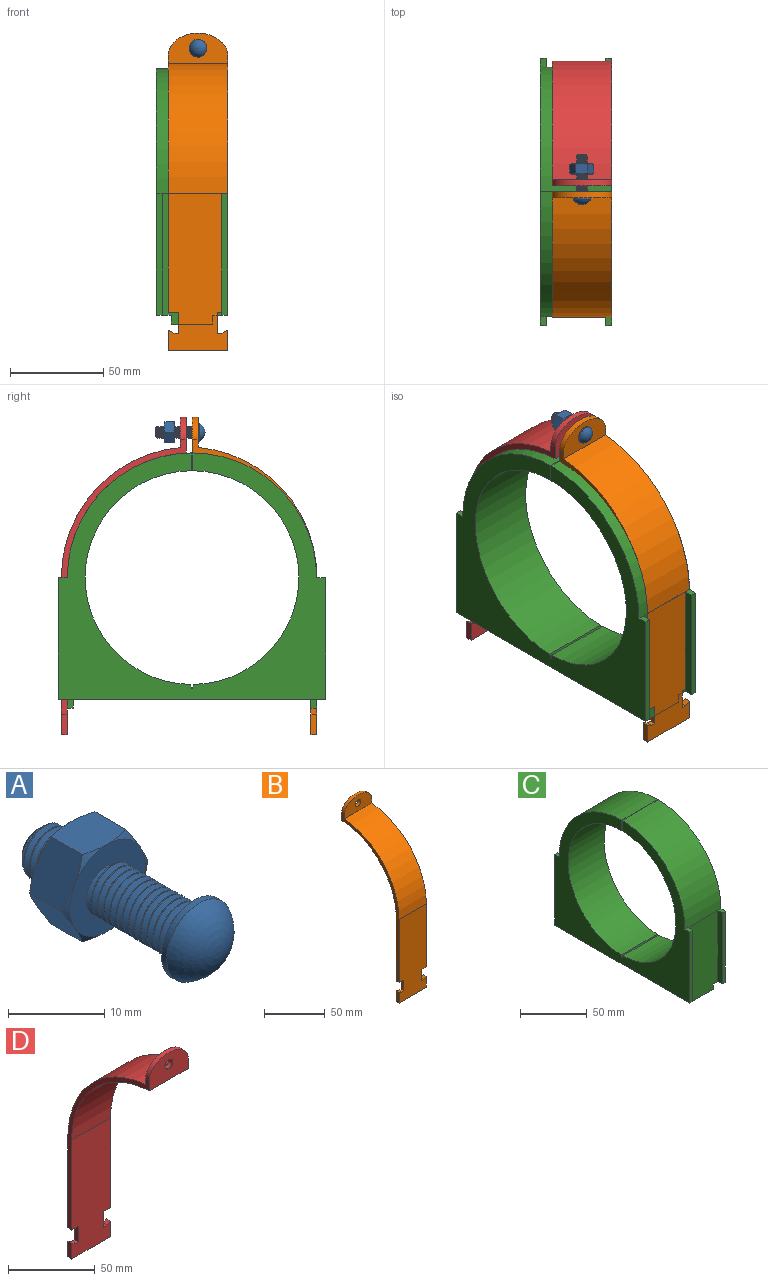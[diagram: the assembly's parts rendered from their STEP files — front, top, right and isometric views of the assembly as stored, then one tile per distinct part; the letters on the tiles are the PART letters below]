
ASSEMBLY  parts=4 mates=3
PART A: 34 faces, bbox 13.4x27.4x13.4 mm
  f0: cylinder r=3.17mm len=12.7mm, axis (0,-1,0), area 31.8mm2, adj f1,f3,f4,f8
  f1: bspline ~13.49x6.35mm, area 172.8mm2, adj f0,f2,f4,f8
  f2: cylinder r=2.59mm len=12.7mm, axis (0,-1,0), area 25.9mm2, adj f1,f3,f4,f8
  f3: bspline ~13.49x6.35mm, area 172.8mm2, adj f0,f2,f4,f8
  f4: plane 9.89x9.89mm, normal (0,1,0), area 45.1mm2, adj f0,f1,f2,f3,f5
  f5: cylinder r=4.76mm len=9.53mm, axis (0,1,0), area 22.8mm2, adj f4,f6
  f6: sphere r=5.32mm, area 98.5mm2, adj f5
  f7: plane 11.47x11.47mm, normal (0,1,0), area 70.8mm2, adj f15,f16,f17,f18,f19,f20,f30,f31
  f8: plane 11.47x11.47mm, normal (0,-1,0), area 70.8mm2, adj f0,f1,f2,f3,f21,f22,f23,f24
  f9: plane 6.09x6.08mm, normal (-0.87,0,0.5), area 33.4mm2, adj f10,f14,f15,f16,f21,f22
  f10: plane 6.95x6.08mm, normal (0,0,1), area 33.4mm2, adj f9,f11,f15,f20,f21,f26
  f11: plane 6.09x6.08mm, normal (0.87,0,0.5), area 33.4mm2, adj f10,f12,f19,f20,f25,f26
  f12: plane 6.09x6.08mm, normal (0.87,0,-0.5), area 33.4mm2, adj f11,f13,f18,f19,f24,f25
  f13: plane 6.95x6.08mm, normal (0,0,-1), area 33.4mm2, adj f12,f14,f17,f18,f23,f24
  f14: plane 6.09x6.08mm, normal (-0.87,0,-0.5), area 33.4mm2, adj f9,f13,f16,f17,f22,f23
  f15: cone r=5.56mm half-angle=60deg, axis (0,-1,0), area 3mm2, adj f7,f9,f10
  f16: cone r=5.56mm half-angle=60deg, axis (0,-1,0), area 3mm2, adj f7,f9,f14
  f17: cone r=5.56mm half-angle=60deg, axis (0,-1,0), area 3mm2, adj f7,f13,f14
  f18: cone r=5.56mm half-angle=60deg, axis (0,-1,0), area 3mm2, adj f7,f12,f13
  f19: cone r=5.56mm half-angle=60deg, axis (0,-1,0), area 3mm2, adj f7,f11,f12
  f20: cone r=5.56mm half-angle=60deg, axis (0,-1,0), area 3mm2, adj f7,f10,f11
  f21: cone r=5.56mm half-angle=60deg, axis (0,1,0), area 3mm2, adj f8,f9,f10
  f22: cone r=5.56mm half-angle=60deg, axis (0,1,0), area 3mm2, adj f8,f9,f14
  f23: cone r=5.56mm half-angle=60deg, axis (0,1,0), area 3mm2, adj f8,f13,f14
  f24: cone r=5.56mm half-angle=60deg, axis (0,1,0), area 3mm2, adj f8,f12,f13
  f25: cone r=5.56mm half-angle=60deg, axis (0,1,0), area 3mm2, adj f8,f11,f12
  f26: cone r=5.56mm half-angle=60deg, axis (0,1,0), area 3mm2, adj f8,f10,f11
  f27: plane 4.54x4.54mm, normal (0,1,0), area 16.2mm2, adj f28
  f28: cone r=3.17mm half-angle=45deg, axis (0,-1,0), area 12.5mm2, adj f27,f29,f30,f31,f32
  f29: cone r=3.17mm half-angle=45deg, axis (0,-1,0), area 1.7mm2, adj f28,f30,f32,f33
  f30: bspline ~6.35x6.35mm, area 56.5mm2, adj f7,f28,f29,f31,f33
  f31: cylinder r=2.59mm len=5.17mm, axis (0,-1,0), area 9.1mm2, adj f7,f28,f30,f32
  f32: bspline ~6.35x6.35mm, area 56.2mm2, adj f7,f28,f29,f31,f33
  f33: cylinder r=3.17mm len=6.35mm, axis (0,-1,0), area 9.6mm2, adj f7,f29,f30,f32
PART B: 21 faces, bbox 31.8x66.7x169.9 mm
  f0: plane 137.43x66.68mm, normal (-1,0,0), area 545.5mm2, adj f1,f13,f14,f15,f16,f17,f18,f20
  f1: plane 5.55x3.18mm, normal (0,0,-1), area 17.6mm2, adj f0,f2,f13,f16
  f2: plane 11.13x3.18mm, normal (-1,0,0), area 35.3mm2, adj f1,f3,f13,f16
  f3: plane 3.18x2.54mm, normal (0,0,1), area 8.1mm2, adj f2,f4,f13,f16
  f4: plane 3.18x3.01mm, normal (0.47,0,0.89), area 10.8mm2, adj f3,f5,f13,f16
  f5: plane 10.97x3.18mm, normal (-1,0,0), area 34.8mm2, adj f4,f6,f13,f16
  f6: plane 31.75x3.18mm, normal (0,0,-1), area 100.8mm2, adj f5,f7,f13,f16
  f7: plane 10.97x3.18mm, normal (1,0,0), area 34.8mm2, adj f6,f8,f13,f16
  f8: plane 3.18x3.01mm, normal (-0.47,0,0.89), area 10.8mm2, adj f7,f9,f13,f16
  f9: plane 3.18x2.54mm, normal (0,0,1), area 8.1mm2, adj f8,f10,f13,f16
  f10: plane 11.13x3.18mm, normal (1,0,0), area 35.3mm2, adj f9,f11,f13,f16
  f11: plane 5.55x3.18mm, normal (0,0,-1), area 17.6mm2, adj f10,f12,f13,f16
  f12: plane 137.43x66.68mm, normal (1,0,0), area 545.5mm2, adj f11,f13,f14,f15,f16,f17,f18,f20
  f13: plane 84.12x31.75mm, normal (0,-1,0), area 2552.2mm2, adj f0,f1,f2,f3,f4,f5,f6,f7
  f14: plane 31.75x16.18mm, normal (0,-1,0), area 400.8mm2, adj f0,f12,f15,f19,f20
  f15: cylinder r=69.85mm len=69.56mm, axis (1,0,0), area 3281.7mm2, adj f0,f12,f13,f14
  f16: plane 84.12x31.75mm, normal (0,1,0), area 2552.2mm2, adj f0,f1,f2,f3,f4,f5,f6,f7
  f17: cylinder r=66.67mm len=66.6mm, axis (1,0,0), area 3224.4mm2, adj f0,f12,f16,f18
  f18: plane 31.75x19.14mm, normal (0,1,0), area 494.8mm2, adj f0,f12,f17,f19,f20
  f19: cylinder r=3.17mm len=6.35mm, axis (0,-1,0), area 63.3mm2, adj f14,f18
  f20: extruded ~31.75x11.91mm, area 139.3mm2, adj f0,f12,f14,f18
PART C: 35 faces, bbox 38.1x142.9x136.5 mm
  f0: plane 65.09x3.18mm, normal (0,-1,0), area 206.7mm2, adj f1,f11,f25,f30
  f1: plane 4.76x3.18mm, normal (0,0,1), area 15.1mm2, adj f0,f23,f25,f30
  f2: plane 65.09x3.18mm, normal (0,1,0), area 206.7mm2, adj f3,f11,f25,f28
  f3: plane 4.76x3.18mm, normal (0,0,1), area 15.1mm2, adj f2,f14,f25,f28
  f4: plane 65.09x3.18mm, normal (0,-1,0), area 206.7mm2, adj f11,f24,f26,f29
  f5: plane 69.85x31.75mm, normal (0,-1,0), area 2172.1mm2, adj f6,f11,f23,f29,f30,f31,f33
  f6: plane 22.17x3.18mm, normal (0,0,-1), area 70.4mm2, adj f5,f7,f31,f33
  f7: plane 22.17x4.76mm, normal (0,1,0), area 105.6mm2, adj f6,f11,f31,f33
  f8: plane 22.17x4.76mm, normal (0,-1,0), area 105.6mm2, adj f9,f11,f32,f34
  f9: plane 22.17x3.18mm, normal (0,0,-1), area 70.4mm2, adj f8,f10,f32,f34
  f10: plane 69.85x31.75mm, normal (0,1,0), area 2172.1mm2, adj f9,f11,f14,f27,f28,f32,f34
  f11: plane 142.88x38.1mm, normal (0,0,-1), area 5000.3mm2, adj f0,f2,f4,f5,f7,f8,f10,f12
  f12: plane 65.09x3.18mm, normal (0,1,0), area 206.7mm2, adj f11,f13,f26,f27
  f13: plane 4.76x3.18mm, normal (0,0,1), area 15.1mm2, adj f12,f14,f26,f27
  f14: cylinder r=66.67mm len=66.68mm, axis (-1,0,0), area 3985.5mm2, adj f3,f10,f13,f15,f25,f26
  f15: plane 38.1x9.53mm, normal (0,-1,0), area 362.9mm2, adj f14,f16,f25,f26
  f16: cylinder r=57.15mm len=114.3mm, axis (-1,0,0), area 6808.1mm2, adj f15,f17,f25,f26
  f17: plane 38.1x2.11mm, normal (0,-0.99,0.15), area 81.5mm2, adj f16,f18,f25,f26
  f18: plane 38.1x0.39mm, normal (0,-0.25,0.97), area 15.5mm2, adj f17,f19,f25,f26
  f19: plane 38.1x0.39mm, normal (0,0.25,0.97), area 15.5mm2, adj f18,f20,f25,f26
  f20: plane 38.1x2.11mm, normal (0,0.99,0.15), area 81.5mm2, adj f19,f21,f25,f26
  f21: cylinder r=57.15mm len=114.3mm, axis (-1,0,0), area 6808.1mm2, adj f20,f22,f25,f26
  f22: plane 38.1x9.53mm, normal (0,1,0), area 362.9mm2, adj f21,f23,f25,f26
  f23: cylinder r=66.67mm len=66.68mm, axis (-1,0,0), area 3985.5mm2, adj f1,f5,f22,f24,f25,f26
  f24: plane 4.76x3.18mm, normal (0,0,1), area 15.1mm2, adj f4,f23,f26,f29
  f25: plane 142.88x131.76mm, normal (1,0,0), area 6016.8mm2, adj f0,f1,f2,f3,f11,f14,f15,f16
  f26: plane 142.88x131.76mm, normal (-1,0,0), area 6016.8mm2, adj f4,f11,f12,f13,f14,f15,f16,f17
  f27: plane 65.09x4.76mm, normal (1,0,0), area 310mm2, adj f10,f11,f12,f13
  f28: plane 65.09x4.76mm, normal (-1,0,0), area 310mm2, adj f2,f3,f10,f11
  f29: plane 65.09x4.76mm, normal (1,0,0), area 310mm2, adj f4,f5,f11,f24
  f30: plane 65.09x4.76mm, normal (-1,0,0), area 310mm2, adj f0,f1,f5,f11
  f31: plane 4.76x3.18mm, normal (-1,0,0), area 15.1mm2, adj f5,f6,f7,f11
  f32: plane 4.76x3.18mm, normal (-1,0,0), area 15.1mm2, adj f8,f9,f10,f11
  f33: plane 4.76x3.18mm, normal (1,0,0), area 15.1mm2, adj f5,f6,f7,f11
  f34: plane 4.76x3.18mm, normal (1,0,0), area 15.1mm2, adj f8,f9,f10,f11
PART D: 21 faces, bbox 31.8x66.7x169.9 mm
  f0: plane 137.43x66.68mm, normal (-1,0,0), area 545.5mm2, adj f1,f13,f14,f15,f16,f17,f18,f20
  f1: plane 84.13x31.75mm, normal (0,1,0), area 2552.2mm2, adj f0,f2,f3,f4,f5,f6,f7,f8
  f2: plane 137.43x66.68mm, normal (1,0,0), area 545.5mm2, adj f1,f3,f14,f15,f16,f17,f18,f20
  f3: plane 5.55x3.18mm, normal (0,0,-1), area 17.6mm2, adj f1,f2,f4,f14
  f4: plane 11.13x3.18mm, normal (1,0,0), area 35.3mm2, adj f1,f3,f5,f14
  f5: plane 3.18x2.54mm, normal (0,0,1), area 8.1mm2, adj f1,f4,f6,f14
  f6: plane 3.18x3.01mm, normal (-0.47,0,0.89), area 10.8mm2, adj f1,f5,f7,f14
  f7: plane 10.97x3.18mm, normal (1,0,0), area 34.8mm2, adj f1,f6,f8,f14
  f8: plane 31.75x3.18mm, normal (0,0,-1), area 100.8mm2, adj f1,f7,f9,f14
  f9: plane 10.97x3.18mm, normal (-1,0,0), area 34.8mm2, adj f1,f8,f10,f14
  f10: plane 3.18x3.01mm, normal (0.47,0,0.89), area 10.8mm2, adj f1,f9,f11,f14
  f11: plane 3.18x2.54mm, normal (0,0,1), area 8.1mm2, adj f1,f10,f12,f14
  f12: plane 11.13x3.18mm, normal (-1,0,0), area 35.3mm2, adj f1,f11,f13,f14
  f13: plane 5.55x3.18mm, normal (0,0,-1), area 17.6mm2, adj f0,f1,f12,f14
  f14: plane 84.12x31.75mm, normal (0,-1,0), area 2552.2mm2, adj f0,f2,f3,f4,f5,f6,f7,f8
  f15: cylinder r=66.67mm len=66.6mm, axis (1,0,0), area 3224.4mm2, adj f0,f2,f14,f16
  f16: plane 31.75x19.14mm, normal (0,-1,0), area 494.8mm2, adj f0,f2,f15,f19,f20
  f17: cylinder r=69.85mm len=69.56mm, axis (1,0,0), area 3281.7mm2, adj f0,f1,f2,f18
  f18: plane 31.75x16.18mm, normal (0,1,0), area 400.8mm2, adj f0,f2,f17,f19,f20
  f19: cylinder r=3.17mm len=6.35mm, axis (0,-1,0), area 63.3mm2, adj f16,f18
  f20: extruded ~31.75x11.91mm, area 139.3mm2, adj f0,f2,f16,f18
PLACE A t=(-83.5,-32.54,26.35)mm
PLACE B t=(-83.5,-32.54,26.35)mm
PLACE C t=(-86.67,-35.59,26.28)mm
PLACE D t=(-83.5,-35.59,26.28)mm
MATE fastened A.f0 <-> B.f19  axis (0,1,0) through (-83.5,-38.89,104)mm
MATE fastened C.f14 <-> D.f15  axis (1,0,0) through (-67.62,-35.59,26.28)mm
MATE fastened C.f25 <-> B.f12  axis (1,0,0) through (-67.62,-35.72,92.95)mm
